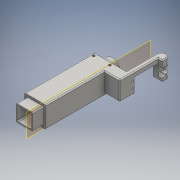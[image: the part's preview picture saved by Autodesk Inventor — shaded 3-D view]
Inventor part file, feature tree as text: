
AUTODESK INVENTOR PART (.ipt)
format: ipt  version: 2016 (Build 200138000, 138)  size: 461,312 bytes
history: native  units: mm
features: extrude x22, sketch x18, fillet x6, projected_geometry x4, other x2
ambient origin geometry x8: Origin, YZ Plane, XZ Plane, XY Plane, X Axis, Y Axis, Z Axis, Center Point
bodies: Body1 (feature_tree), Body2 (feature_tree)
feature tree (52):
  other  "ソリッド1"
  extrude  "押し出し1"  Depth=31.0mm
  fillet  "フィレット1"  Radius=31.0mm
  extrude  "押し出し2"  Depth=20.0mm TaperAngle=0.0deg
  fillet  "フィレット2"  Radius=2.0mm
  extrude  "押し出し3"  Depth=4.5mm
  extrude  "押し出し5"  Depth=4.5mm
  extrude  "押し出し6"  Depth=4.5mm
  extrude  "押し出し7"  Depth=4.5mm
  extrude  "押し出し8"  Depth=30.0mm TaperAngle=0.0deg
  extrude  "押し出し9"  Depth=2.0mm
  extrude  "押し出し10"  Depth=2.0mm
  extrude  "押し出し11"  Depth=2.5mm
  sketch  "スケッチ11"
  extrude  "押し出し12"  Depth=2.5mm
  extrude  "押し出し13"  Depth=2.5mm
  extrude  "押し出し14"  Depth=2.5mm
  extrude  "押し出し15"  Depth=30.0mm TaperAngle=0.0deg
  extrude  "押し出し25"  Depth=2.0mm
  other  "作業平面1"
  extrude  "押し出し29"  Depth=3.0mm
  extrude  "押し出し30"  Depth=3.0mm
  fillet  "フィレット6"  Radius=3.0mm
  extrude  "押し出し35"  Depth=3.0mm
  extrude  "押し出し36"  Depth=90.0mm TaperAngle=0.0deg
  extrude  "押し出し37"  Depth=10.0mm TaperAngle=0.0deg
  extrude  "押し出し38"  Depth=30.0mm
  fillet  "フィレット12"  Radius=15.0mm
  fillet  "フィレット13"  Radius=3.0mm
  extrude  "押し出し39"  Depth=30.0mm TaperAngle=0.0deg
  fillet  "フィレット14"  Radius=20.0mm
  sketch  "スケッチ1"
  sketch  "スケッチ2"
  sketch  "スケッチ3"
  sketch  "スケッチ5"
  sketch  "スケッチ6"
  sketch  "スケッチ7"
  sketch  "スケッチ8"
  sketch  "スケッチ9"
  sketch  "スケッチ10"
  sketch  "スケッチ21"
  sketch  "スケッチ24"
  sketch  "スケッチ25"
  sketch  "スケッチ30"
  projected_geometry  "投影ループ4"
  sketch  "スケッチ31"
  sketch  "スケッチ32"
  projected_geometry  "投影ループ5"
  sketch  "スケッチ35"
  projected_geometry  "投影ループ7"
  projected_geometry  "投影ループ8"
  sketch  "スケッチ36"
